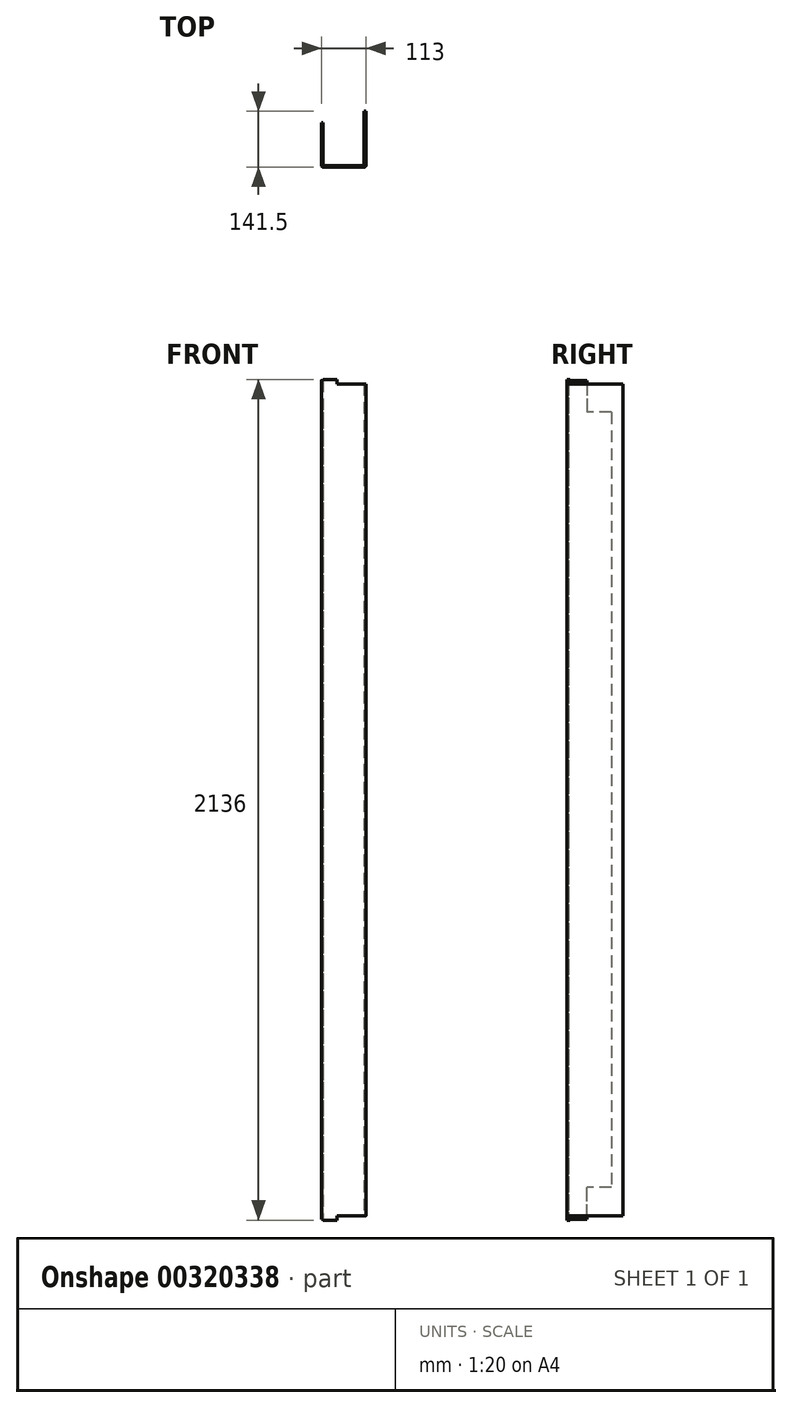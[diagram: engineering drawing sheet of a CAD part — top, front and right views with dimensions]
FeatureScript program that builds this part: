
annotation { "Feature Type Name" : "Feature", "Feature Type Description" : "" }
export const myFeature = defineFeature(function(context is Context, id is Id, definition is map)
    precondition{}
    {
        {
            var Q0;
            Q0=qCreatedBy(makeId("Top.planeOp"),FACE);
            var sketch = newSketch(context, id + "F0", { "sketchPlane" : qUnion([Q0])});
            skLineSegment(sketch, "E0", {"start": v(-59.22, 112.5) * mm, "end": v(-59.22, 4) * mm});
            skLineSegment(sketch, "E1", {"start": v(-55.22, 0) * mm, "end": v(49.78, 0) * mm});
            skLineSegment(sketch, "E2.0", {"start": v(-51.22, 4) * mm, "end": v(44.78, 4) * mm});
            skLineSegment(sketch, "E3", {"start": v(53.78, 4) * mm, "end": v(53.78, 141.5) * mm});
            skLineSegment(sketch, "E4.0", {"start": v(48.78, 8) * mm, "end": v(48.78, 141.5) * mm});
            skArc(sketch, "E5.filletArc", {"start": v(44.78, 4) * mm, "mid": v(47.6, 5.17) * mm, "end": v(48.78, 8) * mm});
            skPoint(sketch, "E6.visualSharp", {"position": v(53.78, 0) * mm});
            skArc(sketch, "E6.filletArc", {"start": v(49.78, 0) * mm, "mid": v(52.6, 1.17) * mm, "end": v(53.78, 4) * mm});
            skPoint(sketch, "E7.visualSharp", {"position": v(-55.22, 4) * mm});
            skArc(sketch, "E7.filletArc", {"start": v(-55.22, 8) * mm, "mid": v(-54.05, 5.17) * mm, "end": v(-51.22, 4) * mm});
            skPoint(sketch, "E8.visualSharp", {"position": v(-59.22, 0) * mm});
            skArc(sketch, "E8.filletArc", {"start": v(-59.22, 4) * mm, "mid": v(-58.05, 1.17) * mm, "end": v(-55.22, 0) * mm});
            skLineSegment(sketch, "E9", {"start": v(48.78, 141.5) * mm, "end": v(53.78, 141.5) * mm});
            skLineSegment(sketch, "E10", {"start": v(-59.22, 112.5) * mm, "end": v(-55.22, 112.5) * mm});
            skLineSegment(sketch, "E11", {"start": v(-55.22, 8) * mm, "end": v(-55.22, 112.5) * mm});
            skSolve(sketch);
        }
        {
            var Q0;
            Q0=qSketchRegion(id+"F0",true);
            extrude(context, id + "F1", {"entities" : qUnion([Q0]), "depth" : 2414 * mm});
        }
        {
            var Q0;
            Q0=makeQuery(id+"F1.opExtrude","SWEPT_FACE",FACE,{"disambiguationData":[OSD([sQuery(id+"F0.wireOp",EDGE,"E1")])]});
            var sketch = newSketch(context, id + "F2", { "sketchPlane" : qUnion([Q0])});
            skLineSegment(sketch, "E12.bottom", {"start": v(145.96, 2414) * mm, "end": v(-20.22, 2414) * mm});
            skLineSegment(sketch, "E12.top", {"start": v(145.96, 2264) * mm, "end": v(-20.22, 2264) * mm});
            skLineSegment(sketch, "E12.left", {"start": v(145.96, 2414) * mm, "end": v(145.96, 2264) * mm});
            skLineSegment(sketch, "E12.right", {"start": v(-20.22, 2414) * mm, "end": v(-20.22, 2264) * mm});
            skLineSegment(sketch, "E13.0", {"start": v(-59.22, 2414) * mm, "end": v(-59.22, 0) * mm});
            skLineSegment(sketch, "E14.0", {"start": v(53.78, 2414) * mm, "end": v(53.78, 0) * mm});
            skLineSegment(sketch, "E15", {"start": v(49.78, 1207) * mm, "end": v(553.52, 1207) * mm});
            skPoint(sketch, "E15.endSnap0", {"position": v(49.78, 1207) * mm});
            skLineSegment(sketch, "E16.MirrorCS", {"start": v(-20.22, 0) * mm, "end": v(-20.22, 150) * mm});
            skLineSegment(sketch, "E17.MirrorCS", {"start": v(145.96, 0) * mm, "end": v(145.96, 150) * mm});
            skLineSegment(sketch, "E18.MirrorCS", {"start": v(145.96, 150) * mm, "end": v(-20.22, 150) * mm});
            skLineSegment(sketch, "E19.MirrorCS", {"start": v(145.96, 0) * mm, "end": v(-20.22, 0) * mm});
            skSolve(sketch);
        }
        {
            var Q0;
            {var subQ0=sQuery(id+"F2.wireOp",EDGE,"E12.left");Q0=makeQuery(id+"F2.imprint","IMPRINT",FACE,{"disambiguationData":[TD([[makeQuery(id+"F2.imprint","IMPRINT",EDGE,{"derivedFrom":subQ0}),-1.0]])]});}
            var Q1;
            {var subQ4=sQuery(id+"F2.wireOp",EDGE,"E12.right");Q1=makeQuery(id+"F2.imprint","IMPRINT",FACE,{"disambiguationData":[TD([[makeQuery(id+"F2.imprint","IMPRINT",EDGE,{"derivedFrom":subQ4}),1.0]])]});}
            var Q2;
            {var subQ0=sQuery(id+"F2.wireOp",EDGE,"E12.bottom");var subQ3=sQuery(id+"F2.wireOp",EDGE,"E14.0");var subQ4=makeQuery(id+"F2.imprint","INTERSECT",VERTEX,{"derivedFrom":[subQ0,subQ3]});Q2=makeQuery(id+"F2.imprint","IMPRINT",FACE,{"disambiguationData":[TD([[makeQuery(id+"F2.imprint","IMPRINT",EDGE,{"disambiguationData":[TD([[subQ4,-1.0]])],"derivedFrom":subQ3}),-1.0]])]});}
            var Q3;
            {var subQ0=sQuery(id+"F2.wireOp",EDGE,"E19.MirrorCS");var subQ1=sQuery(id+"F2.wireOp",EDGE,"E14.0");var subQ2=makeQuery(id+"F2.imprint","INTERSECT",VERTEX,{"derivedFrom":[subQ1,subQ0]});Q3=makeQuery(id+"F2.imprint","IMPRINT",FACE,{"disambiguationData":[TD([[makeQuery(id+"F2.imprint","IMPRINT",EDGE,{"disambiguationData":[TD([[subQ2,1.0]])],"derivedFrom":subQ1}),-1.0]])]});}
            var Q4;
            {var subQ5=sQuery(id+"F2.wireOp",EDGE,"E17.MirrorCS");Q4=makeQuery(id+"F2.imprint","IMPRINT",FACE,{"disambiguationData":[TD([[makeQuery(id+"F2.imprint","IMPRINT",EDGE,{"derivedFrom":subQ5}),1.0]])]});}
            var Q5;
            {var subQ0=sQuery(id+"F2.wireOp",EDGE,"E16.MirrorCS");Q5=makeQuery(id+"F2.imprint","IMPRINT",FACE,{"disambiguationData":[TD([[makeQuery(id+"F2.imprint","IMPRINT",EDGE,{"derivedFrom":subQ0}),-1.0]])]});}
            extrude(context, id + "F3", {"entities" : qUnion([Q0, Q1, Q2, Q3, Q4, Q5]), "operationType" : NewBodyOperationType.REMOVE, "endBound" : BoundingType.THROUGH_ALL, "oppositeDirection" : true, "depth" : 25 * mm});
        }
        {
            var Q0;
            Q0=makeQuery(id+"F1.opExtrude","CAP_FACE",FACE,{"disambiguationData":[OSD([sQuery(id+"F0.wireOp",EDGE,"E0"),sQuery(id+"F0.wireOp",EDGE,"E1"),sQuery(id+"F0.wireOp",EDGE,"E2.0"),sQuery(id+"F0.wireOp",EDGE,"E4.0"),sQuery(id+"F0.wireOp",EDGE,"E3"),sQuery(id+"F0.wireOp",EDGE,"E5.filletArc"),sQuery(id+"F0.wireOp",EDGE,"E6.filletArc"),sQuery(id+"F0.wireOp",EDGE,"E7.filletArc"),sQuery(id+"F0.wireOp",EDGE,"E8.filletArc"),sQuery(id+"F0.wireOp",EDGE,"E9"),sQuery(id+"F0.wireOp",EDGE,"E10"),sQuery(id+"F0.wireOp",EDGE,"E11")])],"isStart":false});
            extrude(context, id + "F4", {"entities" : qUnion([Q0]), "operationType" : NewBodyOperationType.REMOVE, "oppositeDirection" : true, "depth" : 139 * mm});
        }
        {
            var Q0;
            Q0=makeQuery(id+"F1.opExtrude","CAP_FACE",FACE,{"disambiguationData":[OSD([sQuery(id+"F0.wireOp",EDGE,"E0"),sQuery(id+"F0.wireOp",EDGE,"E1"),sQuery(id+"F0.wireOp",EDGE,"E2.0"),sQuery(id+"F0.wireOp",EDGE,"E4.0"),sQuery(id+"F0.wireOp",EDGE,"E3"),sQuery(id+"F0.wireOp",EDGE,"E5.filletArc"),sQuery(id+"F0.wireOp",EDGE,"E6.filletArc"),sQuery(id+"F0.wireOp",EDGE,"E7.filletArc"),sQuery(id+"F0.wireOp",EDGE,"E8.filletArc"),sQuery(id+"F0.wireOp",EDGE,"E9"),sQuery(id+"F0.wireOp",EDGE,"E10"),sQuery(id+"F0.wireOp",EDGE,"E11")])],"isStart":true});
            extrude(context, id + "F5", {"entities" : qUnion([Q0]), "operationType" : NewBodyOperationType.REMOVE, "oppositeDirection" : true, "depth" : 139 * mm});
        }
        {
            var Q0;
            Q0=makeQuery(id+"F1.opExtrude","SWEPT_FACE",FACE,{"disambiguationData":[OSD([sQuery(id+"F0.wireOp",EDGE,"E11")])]});
            var sketch = newSketch(context, id + "F6", { "sketchPlane" : qUnion([Q0])});
            skLineSegment(sketch, "E20.bottom", {"start": v(112.5, 139) * mm, "end": v(50, 139) * mm});
            skLineSegment(sketch, "E20.top", {"start": v(112.5, 222) * mm, "end": v(50, 222) * mm});
            skLineSegment(sketch, "E20.left", {"start": v(112.5, 139) * mm, "end": v(112.5, 222) * mm});
            skLineSegment(sketch, "E20.right", {"start": v(50, 139) * mm, "end": v(50, 222) * mm});
            skLineSegment(sketch, "E21", {"start": v(50, 141) * mm, "end": v(0, 141) * mm});
            skLineSegment(sketch, "E22", {"start": v(0, 141) * mm, "end": v(0, 139) * mm});
            skLineSegment(sketch, "E23", {"start": v(0, 139) * mm, "end": v(50, 139) * mm});
            skLineSegment(sketch, "E24", {"start": v(112.5, 1207) * mm, "end": v(414, 1207) * mm});
            skPoint(sketch, "E24.endSnap0", {"position": v(112.5, 1207) * mm});
            skLineSegment(sketch, "E25.MirrorCS", {"start": v(112.5, 2275) * mm, "end": v(50, 2275) * mm});
            skLineSegment(sketch, "E26.MirrorCS", {"start": v(50, 2273) * mm, "end": v(0, 2273) * mm});
            skLineSegment(sketch, "E27.MirrorCS", {"start": v(0, 2275) * mm, "end": v(50, 2275) * mm});
            skLineSegment(sketch, "E28.MirrorCS", {"start": v(112.5, 2275) * mm, "end": v(112.5, 2192) * mm});
            skLineSegment(sketch, "E29.MirrorCS", {"start": v(112.5, 2192) * mm, "end": v(50, 2192) * mm});
            skLineSegment(sketch, "E30.MirrorCS", {"start": v(50, 2275) * mm, "end": v(50, 2192) * mm});
            skLineSegment(sketch, "E31.MirrorCS", {"start": v(0, 2273) * mm, "end": v(0, 2275) * mm});
            skSolve(sketch);
        }
        {
            var Q0;
            Q0 = qSketchRegion(id + "F6", true);
            extrude(context, id + "F7", {"entities" : qUnion([Q0]), "operationType" : NewBodyOperationType.REMOVE, "oppositeDirection" : true, "depth" : 25 * mm});
        }
    });
